# Revit family: JC KONTAKTER JCK117AT EN
name_source: partatom
category: Specialty Equipment
units: mm (PartAtom-declared; Revit-internal decimal feet)

## family parameters
Cut with Voids When Loaded = No
Enable Cutting in Views = Yes
Host = Face
Maintain Annotation Orientation = Yes
Part Type = Normal
Room Calculation Point = No
Round Connector Dimension = Use Diameter
Shared = No

## types (1)
- JCK117AT
    CE Document = https://jckontakter.se
    Core = Aluminum ENAW 6060
    Default Elevation = 800 mm  [stored 2.62467 ft]
    Description = Stylish, robust elbow switch with flat pressure plate in stainless steel and a core in silver anodized aluminum. The model is developed for use in exclusive environments and in old historical buildings.

It is also available wireless as it is often difficult to run cables in old buildings.
    Endcap = Plastic
    Lid = Stainless steel
    Manufacturer = JC Kontakter
    Manufacturers land = Sweden
    Microswitch = Standard NO IP67
    Minimum rated current = 1mA/4 V DC
    Model = JCK117AT
    Nominal rated current = 12 V - Resistive 6A Inductive L/R 5ms 6A, 24 V - Resistive 6A Inductive L/R 5ms 5A
    Number of microswitches = 2
    Placement information = https://jckontakter.se
    Power factor = 1
    Product datasheet = https://jckontakter.se
    Product weight = 0.410 kg
    URL = https://jckontakter.se
    Voltage = 24 V

note: [stored X ft] marks values corroborated as IEEE doubles in the binary element streams (Revit-internal decimal feet)

## geometry (parser evidence)
native form markers: Sweep x6
no freeform markers — native parametric forms only
